# Revit family: BWY
name_source: partatom
category: Lighting Fixtures
units: mm (PartAtom-declared; Revit-internal decimal feet)

## family parameters
Cut with Voids When Loaded = No
Host = Face
Light Source = Yes
Maintain Annotation Orientation = No
OmniClass Number = 23.80.70.11.14.11
OmniClass Title = Downlights
Part Type = Normal
Room Calculation Point = No
Round Connector Dimension = Use Diameter
Shared = No

## types (18) — shared parameters
Color Filter = 16777215
Default Elevation = 4' - 0"
Description = Suspended Architectual Linear luminaire
Dimming Lamp Color Temperature Shift = <None>
Housing Finish = Metal - Viscor - White
Lamp = LED
Lens Finish = Frosted Acrylic Lens
Manufacturer = Visioneering By Viscor
Model = BWY
Tilt Angle = -90.00°
URL = https://viscor.com
Voltage = 120 V

## per-type parameters (varying)
| type | Apparent Load | Emit from Line Length | Lamp Wattage | Length | Photometric Web File | Width |
| BWY2-P48-LED840K04LFUNV | 14 VA | 3' - 8 1/4" | 14 VA | 3' - 8 1/4" | BWY2-P48-LED840K04LFUNV.ies | 0' - 2" |
| BWY2-P48-LED840K10LFUNV | 34 VA | 3' - 8 1/4" | 34 VA | 3' - 8 1/4" | BWY2-P48-LED840K010LFUNV.ies | 0' - 2" |
| BWY2-P24-LED840K04LFUNV | 7 VA | 1' - 10 1/4" | 7 VA | 1' - 10 1/4" | BWY2-P24-LED840K04LFUNV.ies | 0' - 2" |
| BWY2-P24-LED840K10LFUNV | 17 VA | 1' - 10 1/4" | 17 VA | 1' - 10 1/4" | BWY2-P24-LED840K10LFUNV.ies | 0' - 2" |
| BWY2-P72-LED840K10LFUNV | 51 VA | 5' - 6 1/4" | 51 VA | 5' - 6 1/4" | BWY2-P72-LED840K10LFUNV.ies | 0' - 2" |
| BWY2-P72-LED840K04LFUNV | 21 VA | 5' - 6 1/4" | 21 VA | 5' - 6 1/4" | BWY2-P72-LED840K04LFUNV.ies | 0' - 2" |
| BWY3-P24-LED840K04LFUNV | 6 VA | 1' - 10 1/4" | 6 VA | 1' - 10 1/4" | BWY3-P24-LED840K04LFUNV.ies | 0' - 3" |
| BWY4-P24-LED840K04LFUNV | 6 VA | 1' - 10 1/4" | 6 VA | 1' - 10 1/4" | BWY4-P24-LED840K04LFUNV.ies | 0' - 4" |
| BWY3-P24-LED840K10LFUNV | 16 VA | 1' - 10 1/4" | 16 VA | 1' - 10 1/4" | BWY3-P24-LED840K10LFUNV.ies | 0' - 3" |
| BWY4-P24-LED840K10LFUNV | 15 VA | 1' - 10 1/4" | 15 VA | 1' - 10 1/4" | BWY4-P24-LED840K10LFUNV.ies | 0' - 4" |
| BWY3-P48-LED840K04LFUNV | 12 VA | 3' - 8 1/4" | 12 VA | 3' - 8 1/4" | BWY3-P48-LED840K04LFUNV.ies | 0' - 2" |
| BWY3-P48-LED840K10LFUNV | 31 VA | 3' - 8 1/4" | 31 VA | 3' - 8 1/4" | BWY3-P48-LED840K010LFUNV.ies | 0' - 2" |
| BWY3-P72-LED840K04LFUNV | 19 VA | 5' - 6 1/4" | 19 VA | 5' - 6 1/4" | BWY3-P72-LED840K04LFUNV.ies | 0' - 2" |
| BWY3-P72-LED840K10LFUNV | 47 VA | 5' - 6 1/4" | 47 VA | 5' - 6 1/4" | BWY3-P72-LED840K10LFUNV.ies | 0' - 2" |
| BWY4-P48-LED840K04LFUNV | 12 VA | 3' - 8 1/4" | 12 VA | 3' - 8 1/4" | BWY4-P48-LED840K04LFUNV.ies | 0' - 2" |
| BWY4-P48-LED840K10LFUNV | 30 VA | 3' - 8 1/4" | 30 VA | 3' - 8 1/4" | BWY4-P48-LED840K10LFUNV.ies | 0' - 2" |
| BWY4-P72-LED840K04LFUNV | 18 VA | 5' - 6 1/4" | 18 VA | 5' - 6 1/4" | BWY4-P72-LED840K04LFUNV.ies | 0' - 2" |
| BWY4-P72-LED840K10LFUNV | 45 VA | 5' - 6 1/4" | 45 VA | 5' - 6 1/4" | BWY4-P72-LED840K010LFUNV.ies | 0' - 2" |

## geometry (parser evidence)
native form markers: Sweep x3
no freeform markers — native parametric forms only
